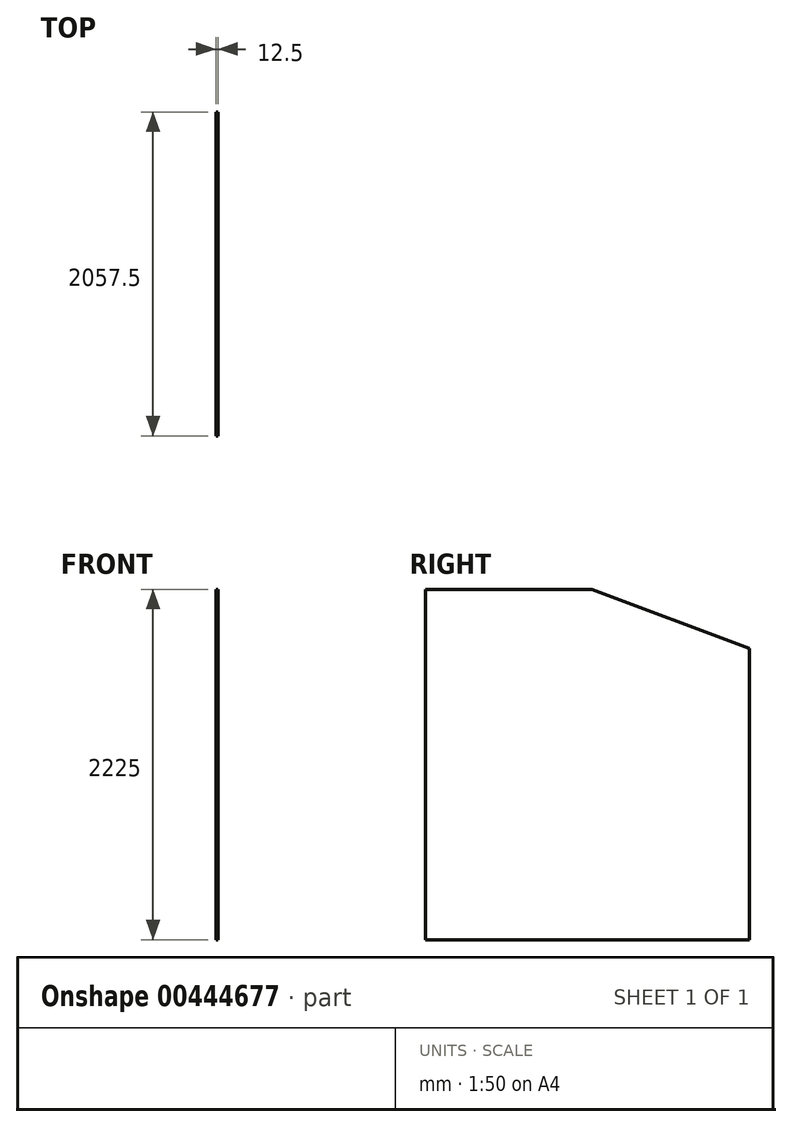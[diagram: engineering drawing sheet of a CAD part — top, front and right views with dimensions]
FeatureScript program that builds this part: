
annotation { "Feature Type Name" : "Feature", "Feature Type Description" : "" }
export const myFeature = defineFeature(function(context is Context, id is Id, definition is map)
    precondition{}
    {
        {
            var Q0;
            Q0=qCreatedBy(makeId("Right.planeOp"),FACE);
            var sketch = newSketch(context, id + "F0", { "sketchPlane" : qUnion([Q0])});
            skLineSegment(sketch, "E0.bottom", {"start": v(0, 0) * mm, "end": v(2057.5, 0) * mm});
            skLineSegment(sketch, "E0.top", {"start": v(0, 2225) * mm, "end": v(1057.5, 2225) * mm});
            skLineSegment(sketch, "E0.left", {"start": v(0, 0) * mm, "end": v(0, 2225) * mm});
            skLineSegment(sketch, "E0.right", {"start": v(2057.5, 0) * mm, "end": v(2057.5, 1850) * mm});
            skLineSegment(sketch, "E1", {"start": v(1057.5, 2225) * mm, "end": v(2057.5, 1850) * mm});
            skPoint(sketch, "E2.orphan", {"position": v(2057.5, 2225) * mm});
            skSolve(sketch);
        }
        {
            var Q0;
            Q0 = qSketchRegion(id + "F0", true);
            extrude(context, id + "F1", {"entities" : qUnion([Q0]), "oppositeDirection" : true, "depth" : 12.5 * mm});
        }
    });
